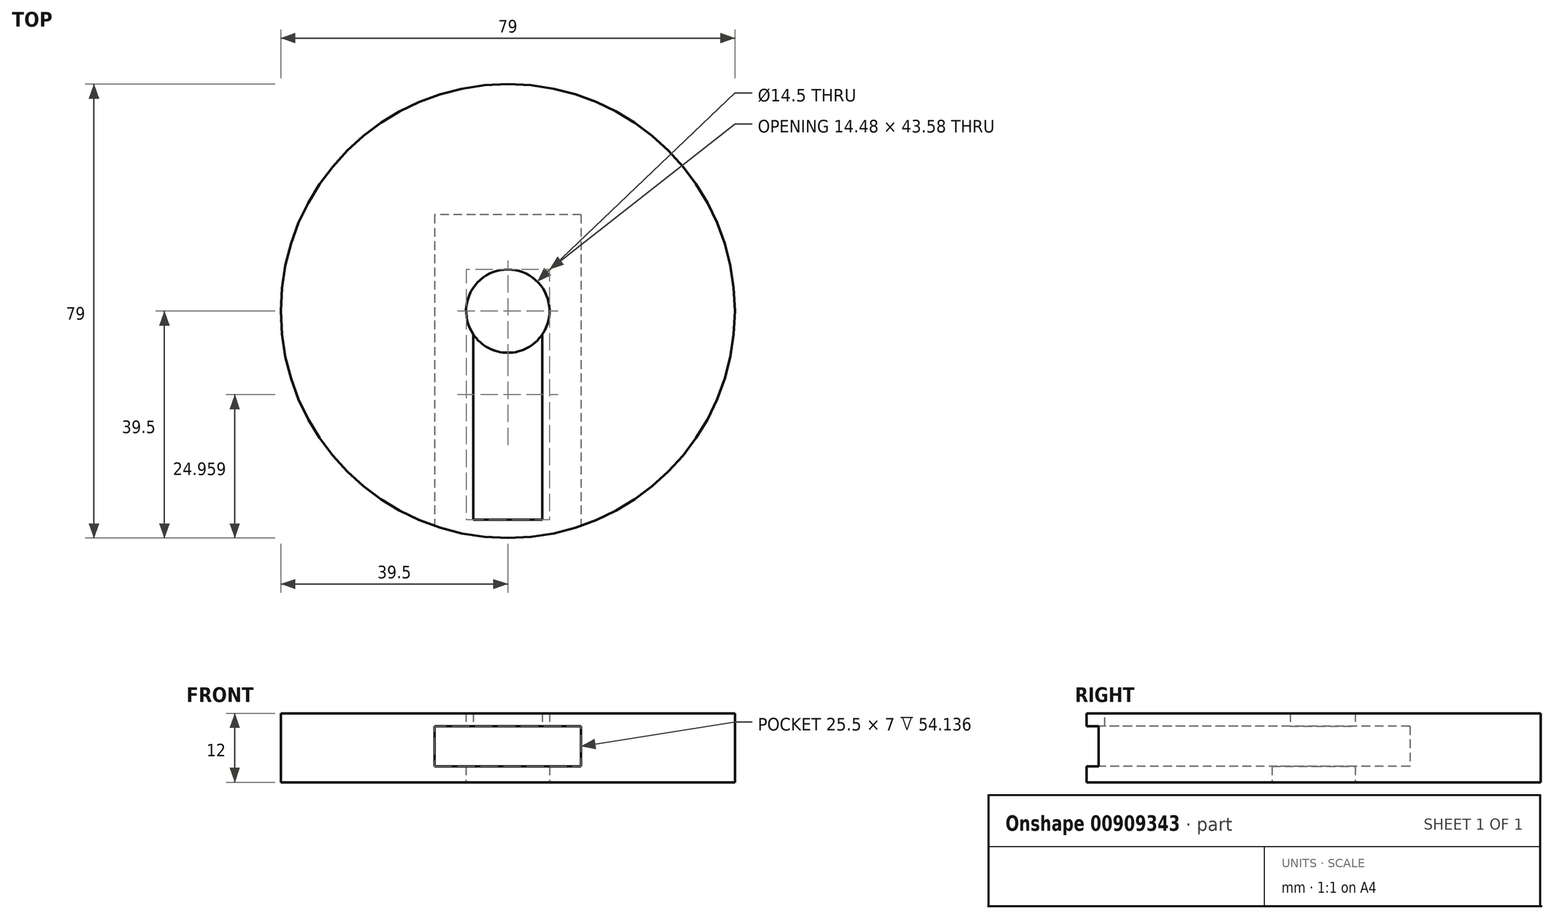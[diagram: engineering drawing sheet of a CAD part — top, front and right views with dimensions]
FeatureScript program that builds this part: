
annotation { "Feature Type Name" : "Feature", "Feature Type Description" : "" }
export const myFeature = defineFeature(function(context is Context, id is Id, definition is map)
    precondition{}
    {
        {
            var Q0;
            Q0=qCreatedBy(makeId("Top.planeOp"),FACE);
            var sketch = newSketch(context, id + "F0", { "sketchPlane" : qUnion([Q0])});
            skCircle(sketch, "E0", {"center": v(0, 0) * mm, "radius": 39.5 * mm});
            skCircle(sketch, "E1", {"center": v(0, 0) * mm, "radius": 7.25 * mm});
            skSolve(sketch);
        }
        {
            var Q0;
            Q0 = qSketchRegion(id + "F0", true);
            extrude(context, id + "F1", {"entities" : qUnion([Q0]), "depth" : 12 * mm, "offsetDistance" : 25 * mm});
        }
        {
            var Q0;
            Q0=makeQuery(id+"F1.opExtrude","CAP_FACE",FACE,{"disambiguationData":[OSD([sQuery(id+"F0.wireOp",EDGE,"E0")])],"isStart":false});
            var sketch = newSketch(context, id + "F2", { "sketchPlane" : qUnion([Q0])});
            skLineSegment(sketch, "E2.bottom", {"start": v(12.75, 16.75) * mm, "end": v(-12.75, 16.75) * mm});
            skLineSegment(sketch, "E2.top", {"start": v(12.75, -50) * mm, "end": v(-12.75, -50) * mm});
            skLineSegment(sketch, "E2.left", {"start": v(12.75, 16.75) * mm, "end": v(12.75, -50) * mm});
            skLineSegment(sketch, "E2.right", {"start": v(-12.75, 16.75) * mm, "end": v(-12.75, -50) * mm});
            skPoint(sketch, "E2.middle", {"position": v(0, -16.62) * mm});
            skSolve(sketch);
        }
        {
            var Q0;
            Q0=qCreatedBy(makeId("Top.planeOp"),FACE);
            cPlane(context, id + "F3", {"entities" : qUnion([Q0]), "cplaneType" : CPlaneType.OFFSET, "offset" : 2.75 * mm, "width" : 150 * mm, "height" : 150 * mm});
        }
        {
            var Q0;
            Q0=qCreatedBy(id+"F3.planeOp",FACE);
            var sketch = newSketch(context, id + "F4", { "sketchPlane" : qUnion([Q0])});
            skLineSegment(sketch, "E3.0", {"start": v(-12.75, 16.75) * mm, "end": v(-12.75, -50) * mm});
            skLineSegment(sketch, "E3.1", {"start": v(12.75, 16.75) * mm, "end": v(-12.75, 16.75) * mm});
            skLineSegment(sketch, "E3.2", {"start": v(12.75, 16.75) * mm, "end": v(12.75, -50) * mm});
            skLineSegment(sketch, "E3.3", {"start": v(12.75, -50) * mm, "end": v(-12.75, -50) * mm});
            skSolve(sketch);
        }
        {
            var Q0;
            Q0 = qSketchRegion(id + "F4", true);
            extrude(context, id + "F5", {"entities" : qUnion([Q0]), "operationType" : NewBodyOperationType.REMOVE, "depth" : 7 * mm, "offsetDistance" : 25 * mm});
        }
        {
            var Q0;
            {var subQ0=sQuery(id+"F2.wireOp",EDGE,"E2.bottom");Q0=makeQuery(id+"F2.imprint","IMPRINT",FACE,{"disambiguationData":[TD([[makeQuery(id+"F2.imprint","IMPRINT",EDGE,{"derivedFrom":subQ0}),-1.0]])]});}
            var sketch = newSketch(context, id + "F6", { "sketchPlane" : qUnion([Q0])});
            skArc(sketch, "E4", {"start": v(6, 0) * mm, "mid": v(0, 6) * mm, "end": v(-6, 0) * mm});
            skLineSegment(sketch, "E5.top", {"start": v(6, -36.33) * mm, "end": v(-6, -36.33) * mm});
            skLineSegment(sketch, "E5.left", {"start": v(6, 0) * mm, "end": v(6, -36.33) * mm});
            skLineSegment(sketch, "E5.right", {"start": v(-6, 0) * mm, "end": v(-6, -36.33) * mm});
            skSolve(sketch);
        }
        {
            var Q0;
            Q0 = qSketchRegion(id + "F6", true);
            extrude(context, id + "F7", {"entities" : qUnion([Q0]), "operationType" : NewBodyOperationType.REMOVE, "oppositeDirection" : true, "depth" : 5 * mm, "offsetDistance" : 25 * mm});
        }
    });
